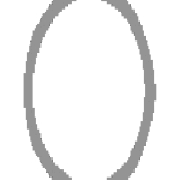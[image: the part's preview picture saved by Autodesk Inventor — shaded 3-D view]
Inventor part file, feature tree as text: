
AUTODESK INVENTOR PART (.ipt)
format: ipt  version: 2021 (Build 250183000, 183)  size: 109,568 bytes
history: native  units: in
note: dims shown in document units (in); Inventor stores cm internally (conversion verified against a paired STEP export)
features: other x4, sketch x3, plane x1
ambient origin geometry x8: Origin, YZ Plane, XZ Plane, XY Plane, X Axis, Y Axis, Z Axis, Center Point
bodies: Solid1 (feature_tree), Body (feature_tree)
feature tree (8):
  other  "Driven Length"
  other  "Frame Generator"
  other  "Start Plane"
  other  "End Plane"
  sketch  "Sketch"  dims[d2=16.0in d4=-0.0in d5=16.0in d6=0.12in d7=0.0in d8=90.0deg d9=16.0in]
  sketch  "Sketch2"  dims[d0=1.0in]
  plane  "Work Plane3"
  sketch  "Sketch3"  dims[d1=0.065in]
